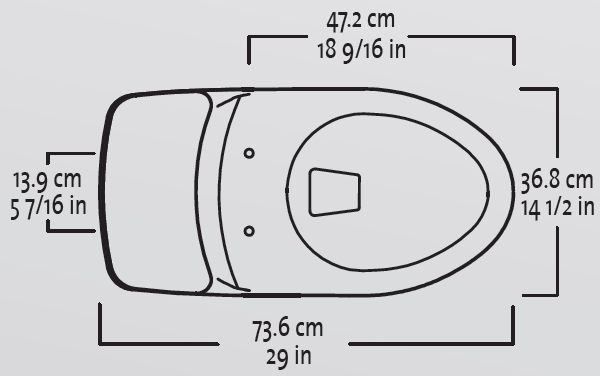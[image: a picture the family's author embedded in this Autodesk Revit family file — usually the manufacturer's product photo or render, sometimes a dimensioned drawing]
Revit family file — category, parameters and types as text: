
# Revit family: O39181001_Sanitario Smart Alongado
name_source: partatom
category: Plumbing Fixtures
units: mm (PartAtom-declared; Revit-internal decimal feet)

## family parameters
Always vertical = Yes
Cut with Voids When Loaded = No
Host = Wall
OmniClass Number = 23.31.19.17
Part Type = Normal
Room Calculation Point = No
Round Connector Dimension = Use Diameter
Shared = No

## types (1)
- Type 1
    Alto = 634 mm  [stored 2.08005 ft]
    Altura de sello = 61 mm. - 2,4 pulg
    Ancho = 368 mm  [stored 1.20735 ft]
    Consumo de agua = 4,8 Lpf. (1,28 Gpf).
    Creado por = BIMBAU
    Default Elevation = 0 mm  [stored 0 ft]
    Description = Diseño compacto y contemporáneo que combina la eficiencia y la optimización de espacio. Sistema de accionamiento Control Azul CORONA de descarga variable para optimizar el consumo de agua, incluye asiento de cierre suave.
    Diámetro = 13 mm
    Diámetro del sifón = 50,8 mm. - 2 pulg
    Espejo de agua = 175 x 255 mm. - 6,88 x 10 pulg
    Fecha de creación = 11/03/2021
    Garantía = Garantía Corona limitada de por vida para la Porcelana-Garantía Grifería limitada de acuerdo a tipologia de Griferia
y Fabricante
    Manufacturer = Corona
    Material = Corona_Porcelana_Vitrea
    Material 2 = Corona_Cromado
    Model = Sanitario Smart Alongado
    Peso  Bruto = 33,2 kg. - 73,2 lb
    Peso neto = 30,6 kg. - 67,46 lb
    Presión de agua = 20 - 80 PSI
    Profundidad = 736 mm  [stored 2.4147 ft]
    Referencia = O39181001
    Sistema de descarga = Descarga sencilla (single.)

note: [stored X ft] marks values corroborated as IEEE doubles in the binary element streams (Revit-internal decimal feet)

## geometry (parser evidence)
native form markers: Sweep x8
no freeform markers — native parametric forms only
